# Revit family: super-g_super-g___l_1750mm_hl_dir_indirekt_led__41_4w_6390lm_3000k_cri_80_dali__430-1562_0b91
name_source: partatom
category: Leuchten
revit_build: Autodesk Revit 2016 (Build: 20190508_0715(x64)
units: mm (PartAtom-declared; Revit-internal decimal feet)

## family parameters
Basisbauteil = Fläche
Beim Laden mit Abzugskörper schneiden = Nein
Bemaßung runder Anschluss = Durchmesser verwenden
Gemeinsam genutzt = Nein
Lichtquelle = Nein
Raumberechnungspunkt = Nein
Teiletyp = Normal

## types (1)
- 430-1562- (9 x LED, 710 lm, 5.1 W, 3000K)
    Approval mark = CE
    Beschreibung = The insert consists of aluminum-extruded profile. Charming SOFT-EDGE design ensure unparalleled styling. The ballast is integrated and allows for an operation with 220-240V (50/60Hz). SUPER-G (# 430-1562) is dimmable via BUS.
    CIE Flux Codes = 48 80 96 61 70
    Color Rendering = 1B/80…89
    Color Temperature = 3000K
    Height = 120 mm
    Hersteller = Prolicht
    Lamp Light Flux = 710 lm
    Lamp Power = 5.1 W
    Lamp count = 9
    Lampe = 9 x LED
    Length = 1750 mm
    Luminous efficacy = 97 lm/W
    ModVariant = Nein
    Modell = 430-1562
    Mounting Place = Ceiling
    Mounting Type = Pendant
    Number of Poles = 1
    OnlyDefault = Ja
    Power Factor = 1
    Product Name = SUPER-G__SUPER-G   L=1750mm HL dir/indirekt LED: 41,4W 6390lm 3000K CRI:80 DALI
    Product group = Suspended profile systems
    ProductGroupID = 944
    Protection Class = Protection class I
    Protection Degree = IP 20
    RLX_Detail_Level = 1
    RlxData = <blob elided: 16313 chars, md5=37a86806>
    Scheinlast = 46 VA
    Socket = socket
    Standby Power = 0 W
    System Light Flux = 4461 lm
    System Power = 46 W
    Typenbild = 430-1562.jpg
    URL = http://relux.com
    VarID = 430-1562-
    Voltage = 0 V
    Vorgabe-Ansicht = 1800 mm
    Weight = 0.00 kg
    Width = 150 mm

## geometry (parser evidence)
native form markers: Blend x4, Sweep x14
no freeform markers — native parametric forms only
